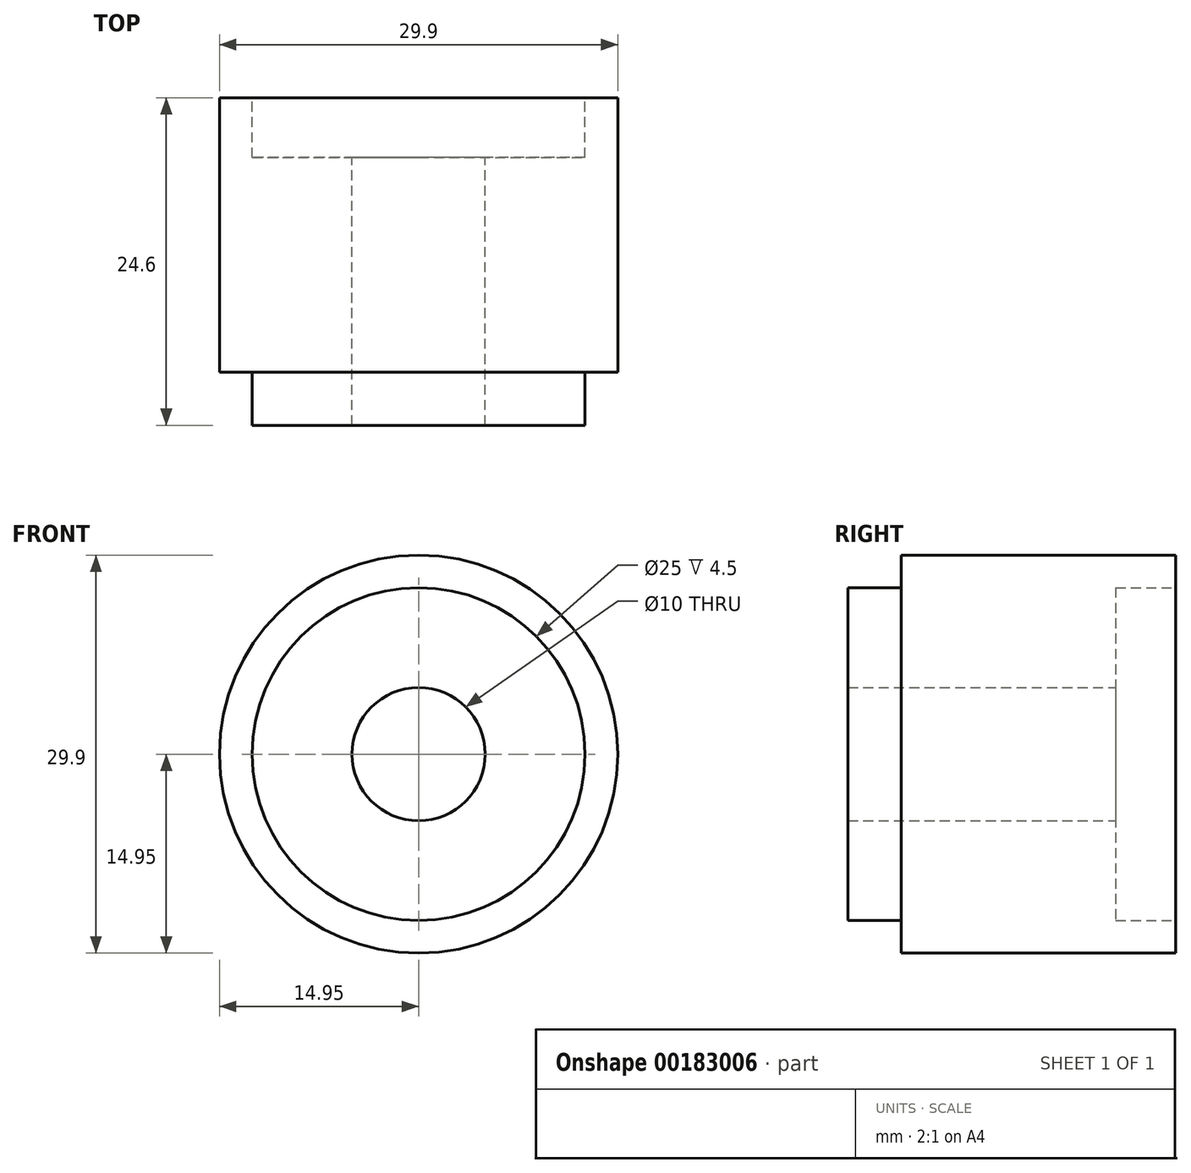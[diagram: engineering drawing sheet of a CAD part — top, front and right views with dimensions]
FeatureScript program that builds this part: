
annotation { "Feature Type Name" : "Feature", "Feature Type Description" : "" }
export const myFeature = defineFeature(function(context is Context, id is Id, definition is map)
    precondition{}
    {
        {
            var Q0;
            Q0=qCreatedBy(makeId("Front.planeOp"),FACE);
            var sketch = newSketch(context, id + "F0", { "sketchPlane" : qUnion([Q0])});
            skCircle(sketch, "E0", {"center": v(0, 0) * mm, "radius": 14.95 * mm});
            skSolve(sketch);
        }
        {
            var Q0;
            Q0=makeQuery(id+"F0.imprint","IMPRINT",FACE,{"disambiguationData":[TD([[makeQuery(id+"F0.imprint","IMPRINT",EDGE,{"derivedFrom":sQuery(id+"F0.wireOp",EDGE,"E0")}),1.0]])]});
            extrude(context, id + "F1", {"entities" : qUnion([Q0]), "depth" : 20.6 * mm});
        }
        {
            var Q0;
            Q0=makeQuery(id+"F1.opExtrude","CAP_FACE",FACE,{"disambiguationData":[OSD([sQuery(id+"F0.wireOp",EDGE,"E0")])],"isStart":false});
            var sketch = newSketch(context, id + "F2", { "sketchPlane" : qUnion([Q0])});
            skCircle(sketch, "E1", {"center": v(0, 0) * mm, "radius": 12.5 * mm});
            skSolve(sketch);
        }
        {
            var Q0;
            Q0=makeQuery(id+"F2.imprint","IMPRINT",FACE,{"disambiguationData":[TD([[makeQuery(id+"F2.imprint","IMPRINT",EDGE,{"derivedFrom":sQuery(id+"F2.wireOp",EDGE,"E1")}),1.0]])]});
            extrude(context, id + "F3", {"entities" : qUnion([Q0]), "operationType" : NewBodyOperationType.ADD, "depth" : 4 * mm});
        }
        {
            var Q0;
            Q0=makeQuery(id+"F1.opExtrude","CAP_FACE",FACE,{"disambiguationData":[OSD([sQuery(id+"F0.wireOp",EDGE,"E0")])],"isStart":true});
            var sketch = newSketch(context, id + "F4", { "sketchPlane" : qUnion([Q0])});
            skCircle(sketch, "E2", {"center": v(0, 0) * mm, "radius": 12.5 * mm});
            skSolve(sketch);
        }
        {
            var Q0;
            Q0=makeQuery(id+"F4.imprint","IMPRINT",FACE,{"disambiguationData":[TD([[makeQuery(id+"F4.imprint","IMPRINT",EDGE,{"derivedFrom":sQuery(id+"F4.wireOp",EDGE,"E2")}),1.0]])]});
            extrude(context, id + "F5", {"entities" : qUnion([Q0]), "operationType" : NewBodyOperationType.REMOVE, "oppositeDirection" : true, "depth" : 4.5 * mm});
        }
        {
            var Q0;
            Q0=makeQuery(id+"F5.boolean.opBoolean","COPY",FACE,{"derivedFrom":makeQuery(id+"F5.opExtrude","CAP_FACE",FACE,{"disambiguationData":[OSD([sQuery(id+"F4.wireOp",EDGE,"E2")])],"isStart":false})});
            var sketch = newSketch(context, id + "F6", { "sketchPlane" : qUnion([Q0])});
            skCircle(sketch, "E3", {"center": v(0, 0) * mm, "radius": 5 * mm});
            skSolve(sketch);
        }
        {
            var Q0;
            Q0=makeQuery(id+"F6.imprint","IMPRINT",FACE,{"disambiguationData":[TD([[makeQuery(id+"F6.imprint","IMPRINT",EDGE,{"derivedFrom":sQuery(id+"F6.wireOp",EDGE,"E3")}),1.0]])]});
            extrude(context, id + "F7", {"entities" : qUnion([Q0]), "operationType" : NewBodyOperationType.REMOVE, "oppositeDirection" : true, "depth" : 25 * mm});
        }
    });
